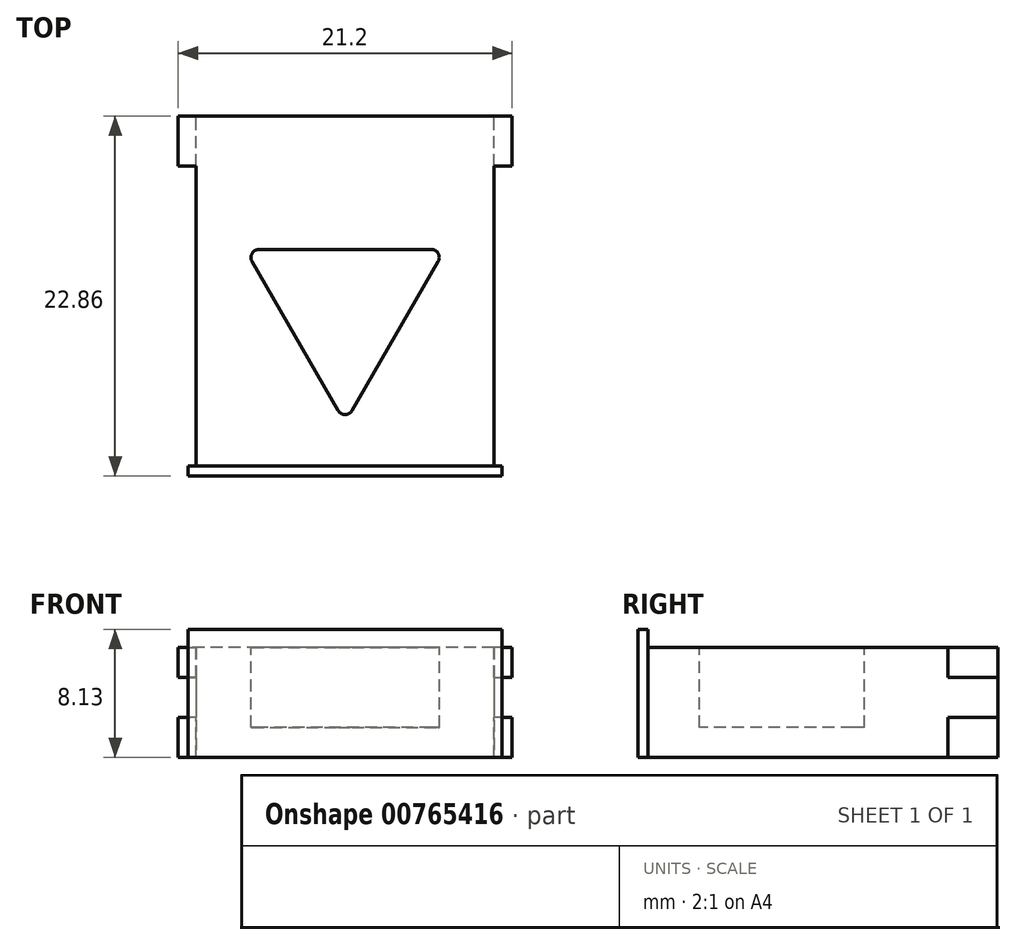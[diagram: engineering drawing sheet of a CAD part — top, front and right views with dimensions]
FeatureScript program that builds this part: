
annotation { "Feature Type Name" : "Feature", "Feature Type Description" : "" }
export const myFeature = defineFeature(function(context is Context, id is Id, definition is map)
    precondition{}
    {
        {
            var Q0;
            Q0=qCreatedBy(makeId("Front.planeOp"),FACE);
            var sketch = newSketch(context, id + "F0", { "sketchPlane" : qUnion([Q0])});
            skLineSegment(sketch, "E0.bottom", {"start": v(9.46, 3.18) * mm, "end": v(-9.46, 3.17) * mm});
            skLineSegment(sketch, "E0.top", {"start": v(9.46, -3.8) * mm, "end": v(-9.46, -3.81) * mm});
            skLineSegment(sketch, "E0.left", {"start": v(9.46, 3.18) * mm, "end": v(9.46, -3.8) * mm});
            skLineSegment(sketch, "E0.right", {"start": v(-9.46, 3.17) * mm, "end": v(-9.46, -3.81) * mm});
            skPoint(sketch, "E0.middle", {"position": v(0, 0) * mm});
            skSolve(sketch);
        }
        {
            var Q0;
            Q0=makeQuery(id+"F0.imprint","IMPRINT",FACE,{"disambiguationData":[TD([[makeQuery(id+"F0.imprint","IMPRINT",EDGE,{"derivedFrom":sQuery(id+"F0.wireOp",EDGE,"E0.bottom")}),1.0]])]});
            extrude(context, id + "F1", {"entities" : qUnion([Q0]), "depth" : 22.86 * mm, "offsetDistance" : 25.4 * mm});
        }
        {
            var Q0;
            Q0=makeQuery(id+"F1.opExtrude","CAP_FACE",FACE,{"disambiguationData":[OSD([sQuery(id+"F0.wireOp",EDGE,"E0.bottom"),sQuery(id+"F0.wireOp",EDGE,"E0.top"),sQuery(id+"F0.wireOp",EDGE,"E0.left"),sQuery(id+"F0.wireOp",EDGE,"E0.right")])],"isStart":false});
            var sketch = newSketch(context, id + "F2", { "sketchPlane" : qUnion([Q0])});
            skLineSegment(sketch, "E1.0", {"start": v(-9.97, 4.32) * mm, "end": v(-9.97, -3.81) * mm});
            skLineSegment(sketch, "E1.1", {"start": v(9.98, 4.32) * mm, "end": v(-9.97, 4.32) * mm});
            skLineSegment(sketch, "E1.2", {"start": v(9.98, 4.32) * mm, "end": v(9.98, -3.8) * mm});
            skLineSegment(sketch, "E1.3", {"start": v(9.98, -3.8) * mm, "end": v(-9.97, -3.81) * mm});
            skSolve(sketch);
        }
        {
            var Q0;
            Q0=makeQuery(id+"F2.imprint","IMPRINT",FACE,{"disambiguationData":[TD([[makeQuery(id+"F2.imprint","IMPRINT",EDGE,{"derivedFrom":sQuery(id+"F2.wireOp",EDGE,"E1.0")}),1.0]])]});
            extrude(context, id + "F3", {"entities" : qUnion([Q0]), "operationType" : NewBodyOperationType.ADD, "oppositeDirection" : true, "depth" : 0.64 * mm, "offsetDistance" : 25.4 * mm});
        }
        {
            var Q0;
            Q0=makeQuery(id+"F1.opExtrude","SWEPT_FACE",FACE,{"disambiguationData":[OSD([sQuery(id+"F0.wireOp",EDGE,"E0.bottom")])]});
            var sketch = newSketch(context, id + "F4", { "sketchPlane" : qUnion([Q0])});
            skPoint(sketch, "E2", {"position": v(0, -13.97) * mm});
            skLineSegment(sketch, "E3", {"start": v(-9.46, 0) * mm, "end": v(-10.6, 0) * mm});
            skLineSegment(sketch, "E4", {"start": v(-10.6, 0) * mm, "end": v(-10.6, -3.17) * mm});
            skLineSegment(sketch, "E5", {"start": v(-10.6, -3.17) * mm, "end": v(-9.46, -3.17) * mm});
            skLineSegment(sketch, "E6.MirrorCS", {"start": v(9.46, 0) * mm, "end": v(10.6, 0) * mm});
            skLineSegment(sketch, "E7.MirrorCS", {"start": v(10.6, 0) * mm, "end": v(10.6, -3.17) * mm});
            skLineSegment(sketch, "E8.MirrorCS", {"start": v(10.6, -3.17) * mm, "end": v(9.46, -3.17) * mm});
            skLineSegment(sketch, "E9.bottom", {"start": v(5.47, -8.47) * mm, "end": v(-5.47, -8.47) * mm});
            skLineSegment(sketch, "E10", {"start": v(-5.91, -9.23) * mm, "end": v(-0.44, -18.7) * mm});
            skLineSegment(sketch, "E11", {"start": v(0.44, -18.7) * mm, "end": v(5.91, -9.23) * mm});
            skPoint(sketch, "E12", {"position": v(0, -8.47) * mm});
            skPoint(sketch, "E13.visualSharp", {"position": v(0, -19.47) * mm});
            skArc(sketch, "E13.filletArc", {"start": v(-0.44, -18.7) * mm, "mid": v(0, -18.96) * mm, "end": v(0.44, -18.7) * mm});
            skPoint(sketch, "E14.visualSharp", {"position": v(-6.35, -8.47) * mm});
            skArc(sketch, "E14.filletArc", {"start": v(-5.47, -8.47) * mm, "mid": v(-5.91, -8.72) * mm, "end": v(-5.91, -9.23) * mm});
            skPoint(sketch, "E15.visualSharp", {"position": v(6.35, -8.47) * mm});
            skArc(sketch, "E15.filletArc", {"start": v(5.91, -9.23) * mm, "mid": v(5.91, -8.72) * mm, "end": v(5.47, -8.47) * mm});
            skSolve(sketch);
        }
        {
            var Q0;
            Q0=makeQuery(id+"F4.imprint","IMPRINT",FACE,{"disambiguationData":[TD([[makeQuery(id+"F4.imprint","IMPRINT",EDGE,{"derivedFrom":sQuery(id+"F4.wireOp",EDGE,"aHxRyVL1-Kome-zMzx-eloK-K6PUuLpYeDD1")}),1.0]])]});
            var Q1;
            Q1=makeQuery(id+"F4.imprint","IMPRINT",FACE,{"disambiguationData":[TD([[makeQuery(id+"F4.imprint","IMPRINT",EDGE,{"derivedFrom":sQuery(id+"F4.wireOp",EDGE,"E9.bottom")}),1.0]])]});
            extrude(context, id + "F5", {"entities" : qUnion([Q0, Q1]), "operationType" : NewBodyOperationType.REMOVE, "oppositeDirection" : true, "depth" : 5.08 * mm, "offsetDistance" : 25.4 * mm});
        }
        {
            var Q0;
            {var subQ0=sQuery(id+"F4.wireOp",EDGE,"E3");Q0=makeQuery(id+"F4.imprint","IMPRINT",FACE,{"disambiguationData":[TD([[makeQuery(id+"F4.imprint","IMPRINT",EDGE,{"derivedFrom":subQ0}),1.0]])]});}
            var Q1;
            {var subQ0=sQuery(id+"F4.wireOp",EDGE,"E6.MirrorCS");Q1=makeQuery(id+"F4.imprint","IMPRINT",FACE,{"disambiguationData":[TD([[makeQuery(id+"F4.imprint","IMPRINT",EDGE,{"derivedFrom":subQ0}),-1.0]])]});}
            var Q2;
            {var subQ0=sQuery(id+"F2.wireOp",EDGE,"E1.3");Q2=makeQuery(id+"F3.boolean.opBoolean","MERGE",FACE,{"derivedFrom":[makeQuery(id+"F1.opExtrude","SWEPT_FACE",FACE,{"disambiguationData":[OSD([sQuery(id+"F0.wireOp",EDGE,"E0.top")])]}),makeQuery(id+"F3.opExtrude","SWEPT_FACE",FACE,{"disambiguationData":[OSD([subQ0]),TDD([makeQuery(id+"F2.imprint","IMPRINT",EDGE,{"disambiguationData":[TD([[makeQuery(id+"F2.imprint","INTERSECT",VERTEX,{"derivedFrom":[makeQuery(id+"F1.opExtrude","CAP_EDGE",EDGE,{"disambiguationData":[OSD([sQuery(id+"F0.wireOp",EDGE,"E0.left")])],"isStart":false}),subQ0]}),1.0]])],"derivedFrom":subQ0})])]}),makeQuery(id+"F3.opExtrude","SWEPT_FACE",FACE,{"disambiguationData":[OSD([subQ0]),TDD([makeQuery(id+"F2.imprint","IMPRINT",EDGE,{"disambiguationData":[TD([[makeQuery(id+"F2.imprint","INTERSECT",VERTEX,{"derivedFrom":[makeQuery(id+"F1.opExtrude","CAP_EDGE",EDGE,{"disambiguationData":[OSD([sQuery(id+"F0.wireOp",EDGE,"E0.right")])],"isStart":false}),subQ0]}),-1.0]])],"derivedFrom":subQ0})])]})]});}
            extrude(context, id + "F6", {"entities" : qUnion([Q0, Q1]), "operationType" : NewBodyOperationType.ADD, "endBound" : BoundingType.UP_TO_SURFACE, "oppositeDirection" : true, "depth" : 25.4 * mm, "endBoundEntityFace" : qUnion([Q2]), "offsetDistance" : 25.4 * mm});
        }
        {
            var Q0;
            Q0=makeQuery(id+"F0.imprint","IMPRINT",FACE,{"disambiguationData":[TD([[makeQuery(id+"F0.imprint","IMPRINT",EDGE,{"derivedFrom":sQuery(id+"F0.wireOp",EDGE,"E0.bottom")}),1.0]])]});
            var sketch = newSketch(context, id + "F7", { "sketchPlane" : qUnion([Q0])});
            skLineSegment(sketch, "E16", {"start": v(9.46, 1.27) * mm, "end": v(10.6, 1.27) * mm});
            skLineSegment(sketch, "E17", {"start": v(10.6, 1.27) * mm, "end": v(10.6, -1.27) * mm});
            skLineSegment(sketch, "E18", {"start": v(10.6, -1.27) * mm, "end": v(9.46, -1.27) * mm});
            skLineSegment(sketch, "E19.MirrorCS", {"start": v(-9.46, 1.27) * mm, "end": v(-10.6, 1.27) * mm});
            skLineSegment(sketch, "E20.MirrorCS", {"start": v(-10.6, 1.27) * mm, "end": v(-10.6, -1.27) * mm});
            skLineSegment(sketch, "E21.MirrorCS", {"start": v(-10.6, -1.27) * mm, "end": v(-9.46, -1.27) * mm});
            skLineSegment(sketch, "E22", {"start": v(9.46, 1.27) * mm, "end": v(9.46, -1.27) * mm});
            skLineSegment(sketch, "E23.MirrorCS", {"start": v(-9.46, 1.27) * mm, "end": v(-9.46, -1.27) * mm});
            skSolve(sketch);
        }
        {
            var Q0;
            Q0=makeQuery(id+"F7.imprint","IMPRINT",FACE,{"disambiguationData":[TD([[makeQuery(id+"F7.imprint","IMPRINT",EDGE,{"derivedFrom":sQuery(id+"F7.wireOp",EDGE,"E16")}),-1.0]])]});
            var Q1;
            Q1=makeQuery(id+"F7.imprint","IMPRINT",FACE,{"disambiguationData":[TD([[makeQuery(id+"F7.imprint","IMPRINT",EDGE,{"derivedFrom":sQuery(id+"F7.wireOp",EDGE,"E19.MirrorCS")}),1.0]])]});
            extrude(context, id + "F8", {"entities" : qUnion([Q0, Q1]), "operationType" : NewBodyOperationType.REMOVE, "depth" : 12.7 * mm, "offsetDistance" : 25.4 * mm});
        }
    });
